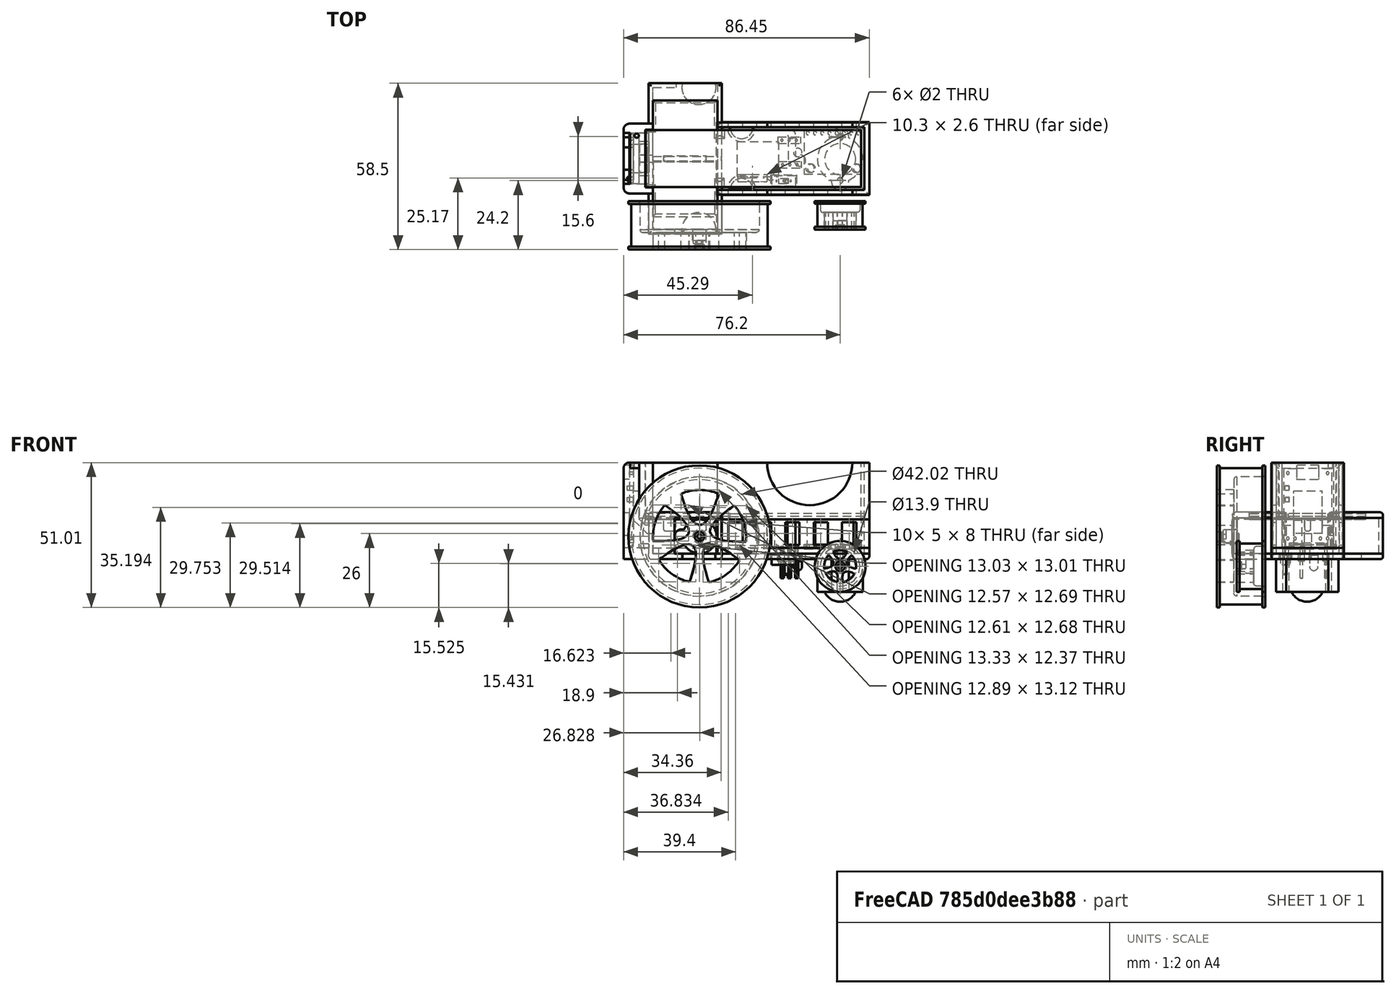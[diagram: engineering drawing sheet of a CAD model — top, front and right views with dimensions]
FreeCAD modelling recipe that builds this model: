
FCSTD DOCUMENT  (FreeCAD 0.18R16146 (Git))
Label: 01_Minibot
License: All rights reserved
LicenseURL: http://en.wikipedia.org/wiki/All_rights_reserved
objects: Part::Box×28, Part::Cylinder×24, Sketcher::SketchObject×20, Part::MultiFuse×20, PartDesign::Body×18, PartDesign::Pad×16, Part::Cut×8, Part::Fillet×7, Part::Chamfer×5, Image::ImagePlane×3, PartDesign::Revolution×2, PartDesign::Pocket×2, PartDesign::PolarPattern×2, Part::Sphere×2, Part::Feature×2, Mesh::Feature×2, Part::Extrusion×1, Part::Part2DObjectPython×1, Part::FeaturePython×1, PartDesign::FeatureBase×1, +1 more types
note: 180 computed .brp shape members not serialized (recipe doc carries the construction recipe); baked Part::Feature solids carry a one-line shape summary decoded from their .brp

FEATURE [Sketcher::SketchObject] Sketch
  MapMode = 5
  Support = -> [XY_Plane]
  sketch-geometry (4):
    g0: LineSegment StartX=-11.1288 StartY=11.9 StartZ=0 EndX=11.1288 EndY=11.9 EndZ=0
    g1: LineSegment StartX=11.1288 StartY=-11.9 StartZ=0 EndX=-11.1288 EndY=-11.9 EndZ=0
    g2: LineSegment StartX=-11.1288 StartY=-11.9 StartZ=0 EndX=-11.1288 EndY=11.9 EndZ=0
    g3: LineSegment StartX=11.1288 StartY=-11.9 StartZ=0 EndX=11.1288 EndY=11.9 EndZ=0
  constraints (9):
    c: Coincident(g0,g2)
    c: Coincident(g3,g1)
    c: Coincident(g3,g0)
    c: Coincident(g1,g2)
    c: Symmetric(g0,g0,g-2)
    c: Symmetric(g1,g0,g-1)
    c: DistanceY(g3,g3) = 23.8
    c: Horizontal(g1)
    c: Vertical(g2)
FEATURE [PartDesign::Pad] Pad
  Length = 12
  Length2 = 100
  Midplane = true
  Profile = -> Sketch
  Type = 0
FEATURE [PartDesign::Body] Body
  Group = -> [Sketch,Pad]
  Origin = -> Origin
  Tip = -> Pad
FEATURE [Sketcher::SketchObject] Sketch003
  MapMode = 5
  Placement = pos=(0,0,0) rot=(1,0,0;1.5708rad)
  Support = -> [XZ_Plane001]
  sketch-geometry (5):
    g0: ArcOfCircle CenterX=-5 CenterY=0 CenterZ=0 NormalX=0 NormalY=0 NormalZ=1 AngleXU=0 Radius=6 StartAngle=0.429754 EndAngle=5.85353
    g1: ArcOfCircle CenterX=1.3 CenterY=0 CenterZ=0 NormalX=0 NormalY=0 NormalZ=1 AngleXU=0 Radius=2.5 StartAngle=4.68906 EndAngle=7.86361
    g2: LineSegment StartX=1.27592 StartY=2.49988 StartZ=0 EndX=0.454409 EndY=2.49988 EndZ=0
    g3: LineSegment StartX=1.24168 StartY=-2.49932 StartZ=0 EndX=0.454668 EndY=-2.49932 EndZ=0
    g4: Circle CenterX=-5 CenterY=0 CenterZ=0 NormalX=0 NormalY=0 NormalZ=1 AngleXU=0 Radius=2.3
  constraints (14):
    c: PointOnObject(g0,g-1)
    c: Radius(g0) = 6
    c: DistanceX(g0) = -5
    c: PointOnObject(g1,g-1)
    c: Radius(g1) = 2.5
    c: DistanceX(g1) = 1.3
    c: Horizontal(g2)
    c: Horizontal(g3)
    c: Coincident(g1,g3)
    c: Coincident(g0,g3)
    c: Coincident(g1,g2)
    c: Coincident(g2,g0)
    c: Coincident(g4,g0)
    c: Radius(g4) = 2.3
FEATURE [PartDesign::Pad] Pad003
  Length = 2.4
  Length2 = 100
  Placement = pos=(0,0,0) rot=(1,0,0;1.5708rad)
  Profile = -> Sketch003
  Type = 0
FEATURE [PartDesign::Body] Body001
  Group = -> [Sketch003,Pad003]
  Origin = -> Origin001
  Placement = pos=(-0.22,13.6,0) rot=(0,0,1;0rad)
  Tip = -> Pad003
FEATURE [Part::Cylinder] Cylinder
  Angle = 360
  AttacherType = Attacher::AttachEngine3D
  Height = 3.2
  Placement = pos=(-5.22,13.6,-3e-15) rot=(-1,0,0;1.5708rad)
  Radius = 2.3
FEATURE [Part::MultiFuse] Fusion  label="Servo9gLeft"
  Placement = pos=(0,13,0) rot=(0,1,0;3.14159rad)
  Shapes = -> [Body,Body001,Cylinder]
FEATURE [Part::Box] Box  label="BatterySlot"
  AttacherType = Attacher::AttachEngine3D
  Height = 20
  Length = 75.8
  Placement = pos=(-13.755,-10,6.01) rot=(0,0,1;0rad)
  Width = 20
FEATURE [Sketcher::SketchObject] Sketch006
  MapMode = 5
  Support = -> [XY_Plane004]
  sketch-geometry (26):
    g0: LineSegment StartX=-13 StartY=8.50414 StartZ=0 EndX=14.2821 EndY=8.50414 EndZ=0
    g1: LineSegment StartX=14.2821 StartY=8.50414 StartZ=0 EndX=14.2821 EndY=6.5 EndZ=0
    g2: LineSegment StartX=14.2821 StartY=-8.50414 StartZ=0 EndX=-13 EndY=-8.50414 EndZ=0
    g3: LineSegment StartX=-13 StartY=-8.50414 StartZ=0 EndX=-13 EndY=-3.9 EndZ=0
    g4: LineSegment StartX=-14.2509 StartY=3.9 StartZ=0 EndX=-13 EndY=3.9 EndZ=0
    g5: LineSegment StartX=-13 StartY=-3.9 StartZ=0 EndX=-14.2509 EndY=-3.9 EndZ=0
    g6: LineSegment StartX=-14.2509 StartY=-3.9 StartZ=0 EndX=-14.2509 EndY=3.9 EndZ=0
    g7: LineSegment StartX=-13 StartY=3.9 StartZ=0 EndX=-13 EndY=8.50414 EndZ=0
    g8: LineSegment StartX=14.2821 StartY=6.5 StartZ=0 EndX=13 EndY=6.5 EndZ=0
    g9: LineSegment StartX=13 StartY=6.5 StartZ=0 EndX=13 EndY=-6.5 EndZ=0
    g10: LineSegment StartX=13 StartY=-6.5 StartZ=0 EndX=14.2821 EndY=-6.5 EndZ=0
    g11: LineSegment StartX=14.2821 StartY=-6.5 StartZ=0 EndX=14.2821 EndY=-8.50414 EndZ=0
    g12: Circle CenterX=-11.5 CenterY=7.00414 CenterZ=0 NormalX=0 NormalY=0 NormalZ=1 AngleXU=0 Radius=0.5
    g13: Circle CenterX=-11.5 CenterY=-7.00414 CenterZ=0 NormalX=0 NormalY=0 NormalZ=1 AngleXU=0 Radius=0.5
    g14: Circle CenterX=11.5 CenterY=7.00414 CenterZ=0 NormalX=0 NormalY=0 NormalZ=1 AngleXU=0 Radius=0.5
    g15: Circle CenterX=11.5 CenterY=4.46414 CenterZ=0 NormalX=0 NormalY=0 NormalZ=1 AngleXU=0 Radius=0.5
    g16: Circle CenterX=11.5 CenterY=-7.00414 CenterZ=0 NormalX=0 NormalY=0 NormalZ=1 AngleXU=0 Radius=0.5
    g17: Circle CenterX=11.5 CenterY=-4.46414 CenterZ=0 NormalX=0 NormalY=0 NormalZ=1 AngleXU=0 Radius=0.5
    g18: LineSegment StartX=-7 StartY=8.00414 StartZ=0 EndX=-5.5 EndY=8.00414 EndZ=0
    g19: LineSegment StartX=-5.5 StartY=8.00414 StartZ=0 EndX=-5.5 EndY=6.50414 EndZ=0
    g20: LineSegment StartX=-5.5 StartY=6.50414 StartZ=0 EndX=-7 EndY=6.50414 EndZ=0
    g21: LineSegment StartX=-7 StartY=6.50414 StartZ=0 EndX=-7 EndY=8.00414 EndZ=0
    g22: LineSegment StartX=-3 StartY=8 StartZ=0 EndX=-1.5 EndY=8 EndZ=0
    g23: LineSegment StartX=-1.5 StartY=8 StartZ=0 EndX=-1.5 EndY=6.5 EndZ=0
    g24: LineSegment StartX=-1.5 StartY=6.5 StartZ=0 EndX=-3 EndY=6.5 EndZ=0
    g25: LineSegment StartX=-3 StartY=6.5 StartZ=0 EndX=-3 EndY=8 EndZ=0
  constraints (68):
    c: Coincident(g0,g1)
    c: Coincident(g11,g2)
    c: Coincident(g2,g3)
    c: Coincident(g7,g0)
    c: Horizontal(g0)
    c: Horizontal(g2)
    c: Vertical(g1)
    c: Vertical(g3)
    c: Symmetric(g0,g11,g-1)
    c: Coincident(g5,g6)
    c: Coincident(g6,g4)
    c: Horizontal(g4)
    c: Horizontal(g5)
    c: Vertical(g6)
    c: Symmetric(g4,g5,g-1)
    c: DistanceX(g4) = -14.2509
    c: DistanceY(g4) = 3.9
    c: PointOnObject(g3,g5)
    c: PointOnObject(g7,g4)
    c: Tangent(g3,g7)
    c: Coincident(g8,g9)
    c: Coincident(g9,g10)
    c: Horizontal(g8)
    c: Horizontal(g10)
    c: Vertical(g9)
    c: Symmetric(g8,g9,g-1)
    c: Coincident(g1,g8)
    c: PointOnObject(g11,g10)
    c: Tangent(g1,g11)
    c: DistanceY(g12,g0) = 1.5
    c: Coincident(g4,g7)
    c: DistanceX(g4) = -13
    c: DistanceX(g0,g12) = 1.5
    c: Radius(g12) = 0.5
    c: Equal(g12,g13) = 0.5
    c: DistanceX(g2,g13) = 1.5
    c: Coincident(g3,g5)
    c: Equal(g2,g0)
    c: DistanceY(g2,g13) = 1.5
    c: Equal(g12,g14) = 0.5
    c: DistanceX(g13,g16) = 23
    c: Vertical(g16,g17)
    c: Vertical(g17,g15)
    c: Vertical(g15,g14)
    c: Horizontal(g12,g14)
    c: DistanceY(g14) = 7.00414
    c: DistanceY(g16,g17) = 2.54
    c: Horizontal(g13,g16)
    c: DistanceY(g15,g14) = 2.54
    c: Coincident(g18,g19)
    c: Coincident(g19,g20)
    c: Coincident(g20,g21)
    c: Coincident(g21,g18)
    c: Horizontal(g18)
    c: Horizontal(g20)
    c: Vertical(g19)
    c: Vertical(g21)
    c: Coincident(g22,g23)
    c: Coincident(g23,g24)
    c: Coincident(g24,g25)
    c: Coincident(g25,g22)
    c: Horizontal(g22)
    c: Horizontal(g24)
    c: Vertical(g23)
    c: Vertical(g25)
    c: DistanceX(g22,g22) = 1.5
    c: DistanceY(g23,g22) = 1.5
    c: Coincident(g10,g11)
FEATURE [Part::Box] Box001  label="Cube"
  AttacherType = Attacher::AttachEngine3D
  Height = 2.5
  Length = 5
  Placement = pos=(-14.25,-3.9,1) rot=(0,0,1;0rad)
  Width = 7.8
FEATURE [PartDesign::Pad] Pad006
  Length = 1.5
  Length2 = 100
  Profile = -> Sketch006
  Type = 0
FEATURE [PartDesign::Body] Body004
  Group = -> [Sketch006,Pad006]
  Origin = -> Origin004
  Tip = -> Pad006
FEATURE [Part::Box] Box002  label="Cube001"
  AttacherType = Attacher::AttachEngine3D
  Height = 1.5
  Length = 2.2
  Placement = pos=(-16.2,-8.005,17.3) rot=(0,0,1;0rad)
  Width = 1.5
FEATURE [Part::Box] Box003  label="Cube002"
  AttacherType = Attacher::AttachEngine3D
  Height = 1.5
  Length = 2.2
  Placement = pos=(-16.2,-8.005,13.3) rot=(0,0,1;0rad)
  Width = 1.5
FEATURE [Part::MultiFuse] Fusion002  label="Re"
  Placement = pos=(-14,-7e-15,11.8) rot=(0.707107,0,-0.707107;3.14159rad)
  Shapes = -> [Body004,Box001]
FEATURE [Part::MultiFuse] Fusion003  label="Recharger"
  Placement = pos=(-4,0,-1) rot=(0,0,1;0rad)
  Shapes = -> [Box002,Box003,Fusion002]
FEATURE [Image::ImagePlane] ImagePlane001
  Placement = pos=(24.2,0,0) rot=(0,0,1;4.71239rad)
  XSize = 80.52
  YSize = 85
FEATURE [Sketcher::SketchObject] Sketch009
  MapMode = 5
  Placement = pos=(0,0,0) rot=(0.57735,0.57735,0.57735;2.0944rad)
  Support = -> [YZ_Plane007]
  sketch-geometry (18):
    g0: LineSegment StartX=-32 StartY=25 StartZ=0 EndX=-31.0063 EndY=25 EndZ=0
    g1: LineSegment StartX=-15.9986 StartY=21.0096 StartZ=0 EndX=-25.0038 EndY=21.0096 EndZ=0
    g2: GeomPoint [constr] X=-32 Y=2 Z=0
    g3: GeomPoint [constr] X=-32 Y=21.9953 Z=0
    g4: LineSegment StartX=-15.9848 StartY=25 StartZ=0 EndX=-15.9848 EndY=24 EndZ=0
    g5: LineSegment StartX=-31.0063 StartY=24 StartZ=0 EndX=-31.0063 EndY=25 EndZ=0
    g6: LineSegment StartX=-15.9848 StartY=25 StartZ=0 EndX=-14.9848 EndY=25 EndZ=0
    g7: LineSegment StartX=-32 StartY=25 StartZ=0 EndX=-32 EndY=1.7 EndZ=0
    g8: LineSegment StartX=-30.3779 StartY=0.8 StartZ=0 EndX=-28.7779 EndY=0.8 EndZ=0
    g9: LineSegment StartX=-28.7779 StartY=0.8 StartZ=0 EndX=-28.7779 EndY=2.4 EndZ=0
    g10: LineSegment StartX=-28.7779 StartY=2.4 StartZ=0 EndX=-25.9779 EndY=2.4 EndZ=0
    g11: LineSegment StartX=-25.9779 StartY=2.4 StartZ=0 EndX=-25.9779 EndY=20.0103 EndZ=0
    g12: ArcOfCircle CenterX=-24.9498 CenterY=19.9825 CenterZ=0 NormalX=0 NormalY=0 NormalZ=1 AngleXU=0 Radius=1.02846 StartAngle=1.62331 EndAngle=3.11452
    g13: ArcOfCircle CenterX=-15.9716 CenterY=21.996 CenterZ=0 NormalX=0 NormalY=0 NormalZ=1 AngleXU=0 Radius=0.986789 StartAngle=4.68499 EndAngle=6.28489
    g14: LineSegment StartX=-14.9848 StartY=25 StartZ=0 EndX=-14.9848 EndY=21.9977 EndZ=0
    g15: LineSegment StartX=-32 StartY=1.7 StartZ=0 EndX=-30.3779 EndY=1.7 EndZ=0
    g16: LineSegment StartX=-30.3779 StartY=1.7 StartZ=0 EndX=-30.3779 EndY=0.8 EndZ=0
    g17: LineSegment StartX=-15.9848 StartY=24 StartZ=0 EndX=-31.0063 EndY=24 EndZ=0
  constraints (39):
    c: Horizontal(g0)
    c: Horizontal(g1)
    c: Coincident(g17,g5)
    c: Vertical(g4)
    c: Vertical(g5)
    c: Coincident(g0,g5)
    c: Vertical(g7)
    c: Horizontal(g8)
    c: Vertical(g9)
    c: Coincident(g10,g9)
    c: Horizontal(g10)
    c: Coincident(g10,g11)
    c: Coincident(g11,g12)
    c: Coincident(g1,g12)
    c: Coincident(g14,g6)
    c: Coincident(g14,g13)
    c: Vertical(g14)
    c: DistanceX(g0) = -32
    c: DistanceY(g0) = 25
    c: DistanceX(g4,g6) = 1
    c: DistanceY(g4,g4) = 1
    c: Coincident(g1,g13)
    c: Vertical(g11)
    c: Coincident(g4,g6)
    c: Horizontal(g6)
    c: DistanceY(g5,g5) = 1
    c: Coincident(g8,g9)
    c: DistanceY(g8) = 0.8
    c: Coincident(g15,g16)
    c: Horizontal(g15)
    c: Vertical(g16)
    c: Coincident(g16,g8)
    c: DistanceX(g8,g8) = 1.6
    c: DistanceY(g16,g16) = 0.9
    c: Coincident(g7,g15)
    c: DistanceX(g10,g10) = 2.8
    c: DistanceY(g10) = 2.4
    c: Coincident(g7,g0)
    c: Coincident(g17,g4)
FEATURE [PartDesign::Revolution] Revolution
  Angle = 360
  Axis = (1.129e-13,1,-1.129e-13)
  Base = (0,0,0)
  Placement = pos=(0,0,0) rot=(0.57735,0.57735,0.57735;2.0944rad)
  Profile = -> Sketch009
  ReferenceAxis = -> Sketch009 [H_Axis]
FEATURE [Sketcher::SketchObject] Sketch010
  Placement = pos=(-5.2,0,0) rot=(1,0,0;1.5708rad)
  sketch-geometry (4):
    g0: ArcOfParabola CenterX=5.21191 CenterY=4.0067 CenterZ=0 NormalX=0 NormalY=0 NormalZ=1 Focal=1.01065 AngleXU=1.56188 StartAngle=-6.6848 EndAngle=6.64864
    g1: GeomPoint X=5.22093 Y=5.0173 Z=0
    g2: LineSegment [constr] StartX=5.21191 StartY=4.0067 StartZ=0 EndX=5.22093 EndY=5.0173 EndZ=0
    g3: ArcOfCircle CenterX=5.32845 CenterY=-0.410138 CenterZ=0 NormalX=0 NormalY=0 NormalZ=1 AngleXU=0 Radius=16.7909 StartAngle=1.16251 EndAngle=1.97913
  constraints (6):
    c: InternalAlignment(g1,g0)
    c: Coincident(g1,g2)
    c: Coincident(g0,g2)
    c: PointOnObject(g3,g0)
    c: Coincident(g0,g3)
    c: Coincident(g3,g0)
FEATURE [PartDesign::Pocket] Pocket
  BaseFeature = -> Revolution
  Length = 5
  Length2 = 100
  Midplane = true
  Placement = pos=(0,0,0) rot=(0.57735,0.57735,0.57735;2.0944rad)
  Profile = -> Sketch010
  Type = 1
FEATURE [PartDesign::PolarPattern] PolarPattern
  Angle = 360
  Axis = -> Y_Axis007
  BaseFeature = -> Pocket
  Occurrences = 5
  Originals = -> [Pocket]
  Placement = pos=(0,0,0) rot=(0.57735,0.57735,0.57735;2.0944rad)
FEATURE [PartDesign::Body] Body007  label="02_Wheel"
  Group = -> [Sketch009,Revolution,Sketch010,Pocket,PolarPattern]
  Origin = -> Origin007
  Placement = pos=(5.2,0,0) rot=(0,0,1;0rad)
  Tip = -> PolarPattern
FEATURE [Sketcher::SketchObject] Sketch012
  MapMode = 5
  Support = -> [XY_Plane010]
  sketch-geometry (8):
    g0: LineSegment StartX=-11.1434 StartY=25 StartZ=0 EndX=-3.10416 EndY=25 EndZ=0
    g1: LineSegment StartX=-3.5631 StartY=-25 StartZ=0 EndX=-11.1434 EndY=-25 EndZ=0
    g2: LineSegment StartX=-11.1434 StartY=-25 StartZ=0 EndX=-11.1434 EndY=25 EndZ=0
    g3: LineSegment StartX=-12.6434 StartY=26.5 StartZ=0 EndX=-3.10416 EndY=26.5 EndZ=0
    g4: LineSegment StartX=-3.5631 StartY=-26.5 StartZ=0 EndX=-12.6434 EndY=-26.5 EndZ=0
    g5: LineSegment StartX=-12.6434 StartY=-26.5 StartZ=0 EndX=-12.6434 EndY=26.5 EndZ=0
    g6: LineSegment StartX=-3.5631 StartY=-25 StartZ=0 EndX=-3.5631 EndY=-26.5 EndZ=0
    g7: LineSegment StartX=-3.10416 StartY=26.5 StartZ=0 EndX=-3.10416 EndY=25 EndZ=0
  constraints (19):
    c: Coincident(g1,g2)
    c: Coincident(g2,g0)
    c: Horizontal(g0)
    c: Horizontal(g1)
    c: Vertical(g2)
    c: Coincident(g4,g5)
    c: Coincident(g5,g3)
    c: Horizontal(g3)
    c: Horizontal(g4)
    c: DistanceX(g3,g0) = 1.5
    c: DistanceY(g0,g3) = 1.5
    c: Vertical(g6)
    c: Coincident(g1,g6)
    c: Coincident(g4,g6)
    c: Vertical(g7)
    c: Coincident(g3,g7)
    c: Coincident(g0,g7)
    c: DistanceY(g4,g1) = 1.5
    c: Symmetric(g4,g3,g-1)
FEATURE [Sketcher::SketchObject] Sketch013
  MapMode = 5
  Support = -> [XY_Plane009]
  sketch-geometry (4):
    g0: LineSegment StartX=11.48 StartY=26.471 StartZ=0 EndX=11.48 EndY=8 EndZ=0
    g1: LineSegment StartX=12.98 StartY=26.471 StartZ=0 EndX=12.98 EndY=8 EndZ=0
    g2: LineSegment StartX=12.98 StartY=26.471 StartZ=0 EndX=11.48 EndY=26.471 EndZ=0
    g3: LineSegment StartX=11.48 StartY=8 StartZ=0 EndX=12.98 EndY=8 EndZ=0
  constraints (11):
    c: Vertical(g0)
    c: Vertical(g1)
    c: Coincident(g2,g1)
    c: Horizontal(g2)
    c: Coincident(g2,g0)
    c: Horizontal(g3)
    c: Coincident(g0,g3)
    c: Coincident(g1,g3)
    c: DistanceX(g0) = 11.48
    c: DistanceY(g0) = 8
    c: DistanceX(g2,g2) = 1.5
FEATURE [PartDesign::Pad] Pad010
  Length = 12.5
  Length2 = 100
  Profile = -> Sketch013
  Type = 0
FEATURE [PartDesign::Body] Body009
  Group = -> [Sketch013,Pad010]
  Origin = -> Origin009
  Tip = -> Pad010
FEATURE [PartDesign::Pad] Pad011
  Length = 12.5
  Length2 = 100
  Profile = -> Sketch012
  Type = 0
FEATURE [PartDesign::Body] Body010
  Group = -> [Sketch012,Pad011]
  Origin = -> Origin010
  Tip = -> Pad011
FEATURE [Part::Box] Box005  label="Cube003"
  AttacherType = Attacher::AttachEngine3D
  Height = 2
  Length = 25.7
  Placement = pos=(-12.5,-26.5,-8) rot=(0,0,1;0rad)
  Width = 53
FEATURE [Sketcher::SketchObject] Sketch016
  MapMode = 5
  Support = -> [XY_Plane013]
  sketch-geometry (10):
    g0: ArcOfCircle CenterX=56.3362 CenterY=0 CenterZ=0 NormalX=0 NormalY=0 NormalZ=1 AngleXU=0 Radius=8 StartAngle=3.52599 EndAngle=5.89879
    g1: ArcOfCircle CenterX=48.3362 CenterY=0 CenterZ=0 NormalX=0 NormalY=0 NormalZ=1 AngleXU=0 Radius=3 StartAngle=1.5708 EndAngle=4.71239
    g2: ArcOfCircle CenterX=64.3402 CenterY=0 CenterZ=0 NormalX=0 NormalY=0 NormalZ=1 AngleXU=0 Radius=3 StartAngle=4.71239 EndAngle=7.85532
    g3: LineSegment StartX=48.3362 StartY=-3 StartZ=0 EndX=48.92 EndY=-3 EndZ=0
    g4: LineSegment StartX=48.3362 StartY=3 StartZ=0 EndX=48.92 EndY=3 EndZ=0
    g5: ArcOfCircle CenterX=56.3362 CenterY=0 CenterZ=0 NormalX=0 NormalY=0 NormalZ=1 AngleXU=0 Radius=8 StartAngle=0.384396 EndAngle=2.7572
    g6: LineSegment StartX=63.7524 StartY=3 StartZ=0 EndX=64.3362 EndY=3 EndZ=0
    g7: LineSegment StartX=63.7524 StartY=-3 StartZ=0 EndX=64.3402 EndY=-3 EndZ=0
    g8: Circle CenterX=48.8362 CenterY=0 CenterZ=0 NormalX=0 NormalY=0 NormalZ=1 AngleXU=0 Radius=1
    g9: Circle CenterX=63.8362 CenterY=0 CenterZ=0 NormalX=0 NormalY=0 NormalZ=1 AngleXU=0 Radius=1
  constraints (26):
    c: PointOnObject(g0,g-1)
    c: Radius(g0) = 8
    c: Tangent(g1,g4) = 1.5708
    c: Tangent(g1,g3) = -1.5708
    c: Coincident(g7,g2) = -1.5708
    c: Coincident(g6,g2) = 1.5708
    c: Horizontal(g3)
    c: Equal(g1,g2)
    c: PointOnObject(g1,g-1)
    c: DistanceX(g0,g2) = 8
    c: DistanceY(g1,g1) = 6
    c: DistanceX(g1,g0) = 8
    c: Equal(g0,g5)
    c: Coincident(g0,g5)
    c: Coincident(g4,g5)
    c: Coincident(g6,g5)
    c: Tangent(g4,g6)
    c: Coincident(g3,g0)
    c: Coincident(g7,g0)
    c: Tangent(g3,g7)
    c: PointOnObject(g8,g-1)
    c: PointOnObject(g9,g-1)
    c: DistanceX(g8,g9) = 15
    c: Distance(g0,g9) = 7.5
    c: Radius(g8) = 1
    c: Radius(g9) = 1
FEATURE [PartDesign::Pad] Pad014
  Length = 11.5
  Length2 = 100
  Profile = -> Sketch016
  Reversed = true
  Type = 0
FEATURE [PartDesign::Body] Body013
  Group = -> [Sketch016,Pad014]
  Origin = -> Origin013
  Tip = -> Pad014
FEATURE [Part::Sphere] Sphere
  Angle1 = -90
  Angle2 = 90
  Angle3 = 360
  AttacherType = Attacher::AttachEngine3D
  Placement = pos=(56.3,0,-9) rot=(0,0,1;0rad)
  Radius = 6
FEATURE [Part::MultiFuse] Fusion006  label="CasterWheel"
  Placement = pos=(54.7,-56.5,-8) rot=(0,0,1;1.5708rad)
  Shapes = -> [Body013,Sphere]
FEATURE [Image::ImagePlane] ImagePlane  label="Recharger_IMG"
  Placement = pos=(-17.5,0,12) rot=(-0.707107,0,0.707107;3.14159rad)
  XSize = 28.5
  YSize = 17
FEATURE [Sketcher::SketchObject] Sketch017
  MapMode = 5
  Support = -> [XY_Plane014]
  sketch-geometry (14):
    g0: LineSegment StartX=21.0792 StartY=7.8 StartZ=0 EndX=41.2792 EndY=7.8 EndZ=0
    g1: LineSegment StartX=41.2792 StartY=7.8 StartZ=0 EndX=41.2792 EndY=-7.8 EndZ=0
    g2: LineSegment StartX=41.2792 StartY=-7.8 StartZ=0 EndX=21.0792 EndY=-7.8 EndZ=0
    g3: LineSegment StartX=21.0792 StartY=-7.8 StartZ=0 EndX=21.0792 EndY=7.8 EndZ=0
    g4: Circle CenterX=23.0792 CenterY=5.78 CenterZ=0 NormalX=0 NormalY=0 NormalZ=1 AngleXU=0 Radius=1.5
    g5: Circle CenterX=39.2792 CenterY=5.78 CenterZ=0 NormalX=0 NormalY=0 NormalZ=1 AngleXU=0 Radius=1.5
    g6: Circle CenterX=40.1024 CenterY=-6.5659 CenterZ=0 NormalX=0 NormalY=0 NormalZ=1 AngleXU=0 Radius=0.6
    g7: Circle CenterX=37.5624 CenterY=-6.5659 CenterZ=0 NormalX=0 NormalY=0 NormalZ=1 AngleXU=0 Radius=0.6
    g8: Circle CenterX=35.0224 CenterY=-6.5659 CenterZ=0 NormalX=0 NormalY=0 NormalZ=1 AngleXU=0 Radius=0.6
    g9: Circle CenterX=32.4824 CenterY=-6.5659 CenterZ=0 NormalX=0 NormalY=0 NormalZ=1 AngleXU=0 Radius=0.6
    g10: Circle CenterX=29.9424 CenterY=-6.5659 CenterZ=0 NormalX=0 NormalY=0 NormalZ=1 AngleXU=0 Radius=0.6
    g11: Circle CenterX=27.4024 CenterY=-6.5659 CenterZ=0 NormalX=0 NormalY=0 NormalZ=1 AngleXU=0 Radius=0.6
    g12: Circle CenterX=24.8624 CenterY=-6.5659 CenterZ=0 NormalX=0 NormalY=0 NormalZ=1 AngleXU=0 Radius=0.6
    g13: Circle CenterX=22.3224 CenterY=-6.5659 CenterZ=0 NormalX=0 NormalY=0 NormalZ=1 AngleXU=0 Radius=0.6
  constraints (39):
    c: Coincident(g0,g1)
    c: Coincident(g1,g2)
    c: Coincident(g2,g3)
    c: Coincident(g3,g0)
    c: Horizontal(g0)
    c: Horizontal(g2)
    c: Vertical(g1)
    c: Vertical(g3)
    c: Symmetric(g0,g2,g-1)
    c: DistanceY(g0) = 7.8
    c: DistanceX(g0,g0) = 20.2
    c: Radius(g4) = 1.5
    c: Equal(g4,g5) = 1.5
    c: Distance(g4,g3) = 2
    c: Distance(g5,g1) = 2
    c: Distance(g4,g0) = 2.02
    c: Distance(g5,g0) = 2.02
    c: Radius(g6) = 0.6
    c: Radius(g7) = 0.6
    c: DistanceX(g7,g6) = 2.54
    c: DistanceY(g6,g7) = 0
    c: Equal(g6,g8) = 0.5
    c: Equal(g7,g9) = 0.5
    c: DistanceX(g9,g8) = 2.54
    c: DistanceY(g8,g9) = 0
    c: DistanceX(g8,g7) = 2.54
    c: Equal(g6,g10) = 0.5
    c: Equal(g7,g11) = 0.5
    c: DistanceX(g11,g10) = 2.54
    c: DistanceY(g10,g11) = 0
    c: Equal(g10,g12) = 0.5
    c: Equal(g11,g13) = 0.5
    c: DistanceX(g13,g12) = 2.54
    c: DistanceY(g12,g13) = 0
    c: DistanceX(g12,g11) = 2.54
    c: DistanceX(g10,g9) = 2.54
    c: DistanceY(g7,g8) = 0
    c: DistanceY(g9,g10) = 0
    c: DistanceY(g12,g11) = 0
FEATURE [PartDesign::Pad] Pad015
  Length = 1.5
  Length2 = 100
  Profile = -> Sketch017
  Reversed = true
  Type = 0
FEATURE [PartDesign::Body] Body014  label="MPU6050"
  Group = -> [Sketch017,Pad015]
  Origin = -> Origin014
  Placement = pos=(21,2.4,-4.4) rot=(1,0,0;3.14159rad)
  Tip = -> Pad015
FEATURE [Image::ImagePlane] ImagePlane002  label="MPU6050_IMG"
  Placement = pos=(31.2,0,-1.6) rot=(0.707107,0.707107,0;3.14159rad)
  XSize = 15.5
  YSize = 20.2
FEATURE [Part::Box] Box007  label="ESP8266-07"
  AttacherType = Attacher::AttachEngine3D
  Height = 1
  Length = 14.7
  Placement = pos=(18.3447,6,-3.08993) rot=(1,0,0;3.14159rad)
  Width = 12.4
FEATURE [Sketcher::SketchObject] Sketch018
  MapMode = 5
  Support = -> [XY_Plane015]
  sketch-geometry (4):
    g0: LineSegment StartX=12.98 StartY=-8 StartZ=0 EndX=11.48 EndY=-8 EndZ=0
    g1: LineSegment StartX=11.48 StartY=-8 StartZ=0 EndX=11.48 EndY=-26.506 EndZ=0
    g2: LineSegment StartX=12.98 StartY=-8 StartZ=0 EndX=12.98 EndY=-26.506 EndZ=0
    g3: LineSegment StartX=11.48 StartY=-26.506 StartZ=0 EndX=12.98 EndY=-26.506 EndZ=0
  constraints (11):
    c: Horizontal(g0)
    c: Coincident(g0,g1)
    c: Coincident(g3,g1)
    c: Coincident(g3,g2)
    c: Horizontal(g3)
    c: Coincident(g0,g2)
    c: DistanceX(g0) = 11.48
    c: DistanceY(g0) = -8
    c: Vertical(g1)
    c: DistanceX(g0,g0) = 1.5
    c: Vertical(g2)
FEATURE [PartDesign::Pad] Pad016
  Length = 12.5
  Length2 = 100
  Profile = -> Sketch018
  Type = 0
FEATURE [PartDesign::Body] Body015
  Group = -> [Sketch018,Pad016]
  Origin = -> Origin015
  Tip = -> Pad016
FEATURE [Part::MultiFuse] Fusion007
  Placement = pos=(0,0,-6) rot=(0,0,1;0rad)
  Shapes = -> [Body015,Body009,Body010]
FEATURE [Part::Box] Box014  label="Cube011"
  AttacherType = Attacher::AttachEngine3D
  Height = 2
  Length = 24.23
  Placement = pos=(-11.25,-0.8,-6) rot=(0,0,1;0rad)
  Width = 1.6
FEATURE [Part::Box] Box015  label="Cube012"
  AttacherType = Attacher::AttachEngine3D
  Height = 5
  Length = 24.23
  Placement = pos=(-16,-1.25,-4) rot=(0,0,1;0rad)
  Width = 2.5
FEATURE [Part::Fillet] Fillet
  Base = -> Box005
  Edges = 4 edges r=1: [Edge4,Edge8,Edge9,Edge11]
  Placement = pos=(-0.2,0,0) rot=(0,0,1;0rad)
FEATURE [Part::Box] Box016  label="Cube013"
  AttacherType = Attacher::AttachEngine3D
  Height = 10
  Length = 2
  Placement = pos=(-18,-4.99,6) rot=(0,0,1;0rad)
  Width = 10
FEATURE [Part::Box] Box017  label="Cube014"
  AttacherType = Attacher::AttachEngine3D
  Height = 1.95
  Length = 3.2
  Placement = pos=(-19.2,-12.33,24.05) rot=(0,0,1;0rad)
  Width = 24.54
FEATURE [Sketcher::SketchObject] Sketch019
  MapMode = 5
  Placement = pos=(0,0,0) rot=(0.57735,0.57735,0.57735;2.0944rad)
  Support = -> [YZ_Plane016]
  sketch-geometry (9):
    g0: LineSegment StartX=9 StartY=26 StartZ=0 EndX=9 EndY=-3.93885 EndZ=0
    g1: LineSegment StartX=9 StartY=-3.93885 StartZ=0 EndX=-9 EndY=-3.93885 EndZ=0
    g2: LineSegment StartX=-9 StartY=-3.93885 StartZ=0 EndX=-9 EndY=26 EndZ=0
    g3: LineSegment StartX=-12.3284 StartY=26 StartZ=0 EndX=-9 EndY=26 EndZ=0
    g4: LineSegment StartX=12.2099 StartY=26 StartZ=0 EndX=12.2099 EndY=-8 EndZ=0
    g5: LineSegment StartX=12.2099 StartY=-8 StartZ=0 EndX=-12.3284 EndY=-8 EndZ=0
    g6: LineSegment StartX=-12.3284 StartY=-8 StartZ=0 EndX=-12.3284 EndY=26 EndZ=0
    g7: LineSegment StartX=9 StartY=26 StartZ=0 EndX=12.2099 EndY=26 EndZ=0
    g8: LineSegment StartX=-9 StartY=0 StartZ=0 EndX=-8.49201 EndY=0 EndZ=0
  constraints (20):
    c: Coincident(g0,g1)
    c: Horizontal(g1)
    c: Vertical(g0)
    c: Vertical(g2)
    c: Symmetric(g2,g0,g-2)
    c: DistanceY(g2) = 26
    c: Coincident(g7,g4)
    c: Coincident(g4,g5)
    c: Coincident(g5,g6)
    c: Coincident(g6,g3)
    c: Horizontal(g3)
    c: Horizontal(g5)
    c: Vertical(g4)
    c: Vertical(g6)
    c: PointOnObject(g3,g2)
    c: PointOnObject(g7,g0)
    c: Tangent(g3,g7)
    c: Coincident(g0,g7)
    c: PointOnObject(g8,g2)
    c: Coincident(g1,g2)
FEATURE [PartDesign::Pad] Pad017
  Length = 5.5
  Length2 = 100
  Placement = pos=(0,0,0) rot=(0.57735,0.57735,0.57735;2.0944rad)
  Profile = -> Sketch019
  Type = 0
FEATURE [PartDesign::Body] Body016
  Group = -> [Sketch019,Pad017]
  Origin = -> Origin016
  Placement = pos=(-21.5,0,0) rot=(0,0,1;0rad)
  Tip = -> Pad017
FEATURE [Part::Box] Box019  label="Cube016"
  AttacherType = Attacher::AttachEngine3D
  Height = 8
  Length = 2
  Placement = pos=(-21.5,-9,0.45) rot=(0,0,1;0rad)
  Width = 1.5
FEATURE [Part::Box] Box020  label="Cube017"
  AttacherType = Attacher::AttachEngine3D
  Height = 8
  Length = 2
  Placement = pos=(-21.5,7.5,0.45) rot=(0,0,1;0rad)
  Width = 1.5
FEATURE [Part::MultiFuse] Fusion008  label="RechargerSupport"
  Shapes = -> [Box020,Box019,Body016,Box017,Box016]
FEATURE [Part::Feature] Face
  shape: bbox 2e-07 x 24.54 x 31.8 mm, 1 faces, 0 solids (baked)
FEATURE [Part::Extrusion] Extrusion
  Base = -> Face
  Dir = (4.5,0,0)
  DirMode = 0
  FaceMakerClass = Part::FaceMakerBullseye
  LengthFwd = 0
  LengthRev = 0
  Solid = true
  Symmetric = false
FEATURE [Part::Part2DObjectPython] Rectangle  # Draft 2D object (typed FeaturePython)
  ChamferSize = 0
  Columns = 1
  FilletRadius = 0
  Height = 26.8106
  Length = 16.3775
  MakeFace = true
  Placement = pos=(-23.2993,-13.6958,6.5) rot=(0,0,1;0rad)
  Rows = 1
FEATURE [Part::Box] Box021  label="Cube018"
  AttacherType = Attacher::AttachEngine3D
  Height = 5
  Length = 5.5
  Placement = pos=(-18,-8.99,1) rot=(0,0,1;0rad)
  Width = 10
FEATURE [Part::Chamfer] Chamfer
  Base = -> Box021
  Edges = 1 edges r=4.8: [Edge4]
  Placement = pos=(0,4,0) rot=(0,0,1;0rad)
FEATURE [Part::Box] Box022  label="Cube019"
  AttacherType = Attacher::AttachEngine3D
  Height = 29
  Length = 22.74
  Placement = pos=(-11.26,-20.5,0) rot=(0,0,1;0rad)
  Width = 41
FEATURE [Part::Box] Box024  label="Cube021"
  AttacherType = Attacher::AttachEngine3D
  Height = 2
  Length = 25.7
  Placement = pos=(-12.5,-26.5,-8) rot=(0,0,1;0rad)
  Width = 53
FEATURE [Part::Fillet] Fillet003
  Base = -> Box024
  Edges = 4 edges r=1: [Edge4,Edge8,Edge9,Edge11]
  Placement = pos=(-0.2,0,0.5) rot=(1,0,0;3.14159rad)
FEATURE [Part::Cylinder] Cylinder009
  Angle = 360
  AttacherType = Attacher::AttachEngine3D
  Height = 25
  Placement = pos=(-16.9,8,3) rot=(0,0,1;0rad)
  Radius = 0.75
FEATURE [Part::Feature] CutVolume
  shape: bbox 9.221 x 27 x 18.3 mm, 6 faces (baked)
FEATURE [Part::Cut] CutPlane
  Base = -> Extrusion
  Tool = -> CutVolume
FEATURE [Part::MultiFuse] Fusion013
  Shapes = -> [Fusion008,Chamfer,CutPlane]
FEATURE [Part::Cut] Cut005
  Base = -> Fusion013
  Placement = pos=(0,0.06,0) rot=(0,0,1;0rad)
  Tool = -> Cylinder009
FEATURE [Sketcher::SketchObject] Sketch011
  MapMode = 5
  Support = -> [XY_Plane008]
  sketch-geometry (8):
    g0: LineSegment StartX=11.488 StartY=11 StartZ=0 EndX=63.2 EndY=11 EndZ=0
    g1: LineSegment StartX=63.2 StartY=11 StartZ=0 EndX=63.2 EndY=-11 EndZ=0
    g2: LineSegment StartX=63.2 StartY=-11 StartZ=0 EndX=11.488 EndY=-11 EndZ=0
    g3: LineSegment StartX=11.488 StartY=12.75 StartZ=0 EndX=64.95 EndY=12.75 EndZ=0
    g4: LineSegment StartX=64.95 StartY=12.75 StartZ=0 EndX=64.95 EndY=-12.75 EndZ=0
    g5: LineSegment StartX=64.95 StartY=-12.75 StartZ=0 EndX=11.488 EndY=-12.75 EndZ=0
    g6: LineSegment StartX=11.488 StartY=12.75 StartZ=0 EndX=11.488 EndY=11 EndZ=0
    g7: LineSegment StartX=11.488 StartY=-12.75 StartZ=0 EndX=11.488 EndY=-11 EndZ=0
  constraints (21):
    c: Coincident(g0,g1)
    c: Coincident(g1,g2)
    c: Horizontal(g0)
    c: Horizontal(g2)
    c: Vertical(g1)
    c: Coincident(g3,g4)
    c: Coincident(g4,g5)
    c: Horizontal(g3)
    c: Horizontal(g5)
    c: Vertical(g4)
    c: DistanceX(g1) = 63.2
    c: DistanceX(g1,g4) = 1.75
    c: DistanceY(g4,g1) = 1.75
    c: DistanceY(g0) = 11
    c: Symmetric(g0,g2,g-1)
    c: Symmetric(g3,g5,g-1)
    c: Coincident(g6,g3)
    c: Coincident(g6,g0)
    c: Vertical(g6)
    c: Coincident(g7,g5)
    c: Coincident(g7,g2)
FEATURE [PartDesign::Pad] Pad009
  Length = 20
  Length2 = 100
  Profile = -> Sketch011
  Type = 0
FEATURE [PartDesign::Body] Body008
  Group = -> [Sketch011,Pad009]
  Origin = -> Origin008
  Placement = pos=(0,0,6) rot=(0,0,1;0rad)
  Tip = -> Pad009
FEATURE [Part::MultiFuse] Fusion014
  Shapes = -> [Fillet003,Body008]
FEATURE [Part::Cylinder] Cylinder010
  Angle = 360
  AttacherType = Attacher::AttachEngine3D
  Height = 20
  Placement = pos=(5,-25,-11) rot=(0,0,1;0rad)
  Radius = 6
FEATURE [Part::Cylinder] Cylinder011
  Angle = 360
  AttacherType = Attacher::AttachEngine3D
  Height = 20
  Placement = pos=(5,25,-11) rot=(0,0,1;0rad)
  Radius = 6
FEATURE [Part::MultiFuse] Fusion015
  Shapes = -> [Cylinder010,Cylinder011]
FEATURE [Part::Cut] Cut007
  Base = -> Fillet
  Tool = -> Fusion015
FEATURE [Part::Box] Box026  label="Cube023"
  AttacherType = Attacher::AttachEngine3D
  Height = 2
  Length = 16
  Placement = pos=(11.48,8,-6) rot=(0,0,-1;1.5708rad)
  Width = 1.5
FEATURE [Part::Cylinder] Cylinder014
  Angle = 360
  AttacherType = Attacher::AttachEngine3D
  Height = 11.2
  Placement = pos=(-46,-6,1.1) rot=(-1,0,0;1.5708rad)
  Radius = 0.4
FEATURE [Part::Box] Box031  label="Cube027"
  AttacherType = Attacher::AttachEngine3D
  Height = 2.2
  Length = 8
  Placement = pos=(-52.54,0,0) rot=(0,0,1;0rad)
  Width = 2.4
FEATURE [Part::Cylinder] Cylinder015
  Angle = 360
  AttacherType = Attacher::AttachEngine3D
  Height = 11.2
  Placement = pos=(-48.54,-6,1.1) rot=(-1,0,0;1.5708rad)
  Radius = 0.4
FEATURE [Part::Fillet] Fillet005
  Base = -> Box014
  Edges = 2 edges r=0.5: [Edge10,Edge12]
FEATURE [Sketcher::SketchObject] Sketch022
  MapMode = 5
  Placement = pos=(0,0,0) rot=(1,0,0;1.5708rad)
  Support = -> [XZ_Plane019]
  sketch-geometry (8):
    g0: LineSegment StartX=-4.25 StartY=1.75 StartZ=0 EndX=4.25 EndY=1.75 EndZ=0
    g1: LineSegment StartX=4.25 StartY=1.75 StartZ=0 EndX=4.25 EndY=-1.75 EndZ=0
    g2: LineSegment StartX=4.25 StartY=-1.75 StartZ=0 EndX=-4.25 EndY=-1.75 EndZ=0
    g3: LineSegment StartX=-4.25 StartY=-1.75 StartZ=0 EndX=-4.25 EndY=1.75 EndZ=0
    g4: LineSegment StartX=-1.8 StartY=0.82 StartZ=0 EndX=1.8 EndY=0.82 EndZ=0
    g5: LineSegment StartX=1.8 StartY=0.82 StartZ=0 EndX=1.8 EndY=-0.82 EndZ=0
    g6: LineSegment StartX=1.8 StartY=-0.82 StartZ=0 EndX=-1.8 EndY=-0.82 EndZ=0
    g7: LineSegment StartX=-1.8 StartY=-0.82 StartZ=0 EndX=-1.8 EndY=0.82 EndZ=0
  constraints (24):
    c: Coincident(g0,g1)
    c: Coincident(g1,g2)
    c: Coincident(g2,g3)
    c: Coincident(g3,g0)
    c: Horizontal(g0)
    c: Horizontal(g2)
    c: Vertical(g1)
    c: Vertical(g3)
    c: Symmetric(g0,g2,g-1)
    c: Symmetric(g0,g0,g-2)
    c: DistanceY(g3,g3) = 3.5
    c: DistanceX(g2,g2) = 8.5
    c: Coincident(g4,g5)
    c: Coincident(g5,g6)
    c: Coincident(g6,g7)
    c: Coincident(g7,g4)
    c: Horizontal(g4)
    c: Horizontal(g6)
    c: Vertical(g5)
    c: Vertical(g7)
    c: Symmetric(g4,g4,g-2)
    c: Symmetric(g6,g4,g-1)
    c: DistanceX(g4,g4) = 3.6
    c: DistanceY(g5,g5) = 1.64
FEATURE [PartDesign::Pad] Pad020
  Length = 3.5
  Length2 = 100
  Placement = pos=(0,0,0) rot=(1,0,0;1.5708rad)
  Profile = -> Sketch022
  Type = 0
FEATURE [PartDesign::Body] Body019
  Group = -> [Sketch022,Pad020]
  Origin = -> Origin019
  Tip = -> Pad020
FEATURE [Part::Box] Box049  label="Cube045"
  AttacherType = Attacher::AttachEngine3D
  Height = 1.5
  Length = 1.5
  Placement = pos=(0.3,-7,-0.75) rot=(0,0,1;0rad)
  Width = 7
FEATURE [Part::Chamfer] Chamfer004
  Base = -> Box049
  Edges = 4 edges r=0.3: [Edge1,Edge5,Edge9,Edge10]
FEATURE [Part::Cylinder] Cylinder030
  Angle = 360
  AttacherType = Attacher::AttachEngine3D
  Height = 3.7
  Placement = pos=(0,-0.05,0) rot=(-1,0,0;1.5708rad)
  Radius = 0.25
FEATURE [Part::Cylinder] Cylinder031
  Angle = 360
  AttacherType = Attacher::AttachEngine3D
  Height = 3.7
  Placement = pos=(2.5,-0.05,0) rot=(-1,0,0;1.5708rad)
  Radius = 0.25
FEATURE [Part::Cylinder] Cylinder032
  Angle = 360
  AttacherType = Attacher::AttachEngine3D
  Height = 3.7
  Placement = pos=(-2.5,-0.05,0) rot=(-1,0,0;1.5708rad)
  Radius = 0.25
FEATURE [Part::MultiFuse] Fusion033  label="SlideSwitch"
  Placement = pos=(34.8,-7.9,-0.8) rot=(1,0,0;1.5708rad)
  Shapes = -> [Body019,Cylinder030,Chamfer004,Cylinder032,Cylinder031]
FEATURE [Mesh::Feature] SmartCars  label="SmartCars_V01"
  Placement = pos=(132.5,151,-1.7) rot=(0,0,1;4.71239rad)
FEATURE [Part::Cylinder] Cylinder033
  Angle = 360
  AttacherType = Attacher::AttachEngine3D
  Height = 11.2
  Placement = pos=(-51.08,-6,1.1) rot=(-1,0,0;1.5708rad)
  Radius = 0.4
FEATURE [Part::MultiFuse] Fusion034  label="PinsBarA"
  Placement = pos=(85.28,7.57,-3) rot=(1,0,0;1.5708rad)
  Shapes = -> [Box031,Cylinder033,Cylinder014,Cylinder015]
FEATURE [Part::Cylinder] Cylinder034
  Angle = 360
  AttacherType = Attacher::AttachEngine3D
  Height = 11.2
  Placement = pos=(-51.08,-6,1.1) rot=(-1,0,0;1.5708rad)
  Radius = 0.4
FEATURE [Part::Cylinder] Cylinder035
  Angle = 360
  AttacherType = Attacher::AttachEngine3D
  Height = 11.2
  Placement = pos=(-46,-6,1.1) rot=(-1,0,0;1.5708rad)
  Radius = 0.4
FEATURE [Part::Box] Box050  label="Cube046"
  AttacherType = Attacher::AttachEngine3D
  Height = 2.2
  Length = 8
  Placement = pos=(-52.54,0,0) rot=(0,0,1;0rad)
  Width = 2.4
FEATURE [Part::Cylinder] Cylinder036
  Angle = 360
  AttacherType = Attacher::AttachEngine3D
  Height = 11.2
  Placement = pos=(-48.54,-6,1.1) rot=(-1,0,0;1.5708rad)
  Radius = 0.4
FEATURE [Part::MultiFuse] Fusion035  label="PinsBarB"
  Placement = pos=(85.54,-1.07,-3) rot=(1,0,0;1.5708rad)
  Shapes = -> [Box050,Cylinder034,Cylinder035,Cylinder036]
FEATURE [Part::Cylinder] Cylinder037
  Angle = 360
  AttacherType = Attacher::AttachEngine3D
  Height = 4
  Placement = pos=(39.8,2.1,2.8) rot=(0,0,1;0rad)
  Radius = 1.5
FEATURE [Part::Sphere] Sphere001
  Angle1 = -90
  Angle2 = 90
  Angle3 = 360
  AttacherType = Attacher::AttachEngine3D
  Placement = pos=(39.8,2.1,6.8) rot=(0,0,1;0rad)
  Radius = 1.5
FEATURE [Part::MultiFuse] Fusion036  label="LED"
  Placement = pos=(0,4.25,2) rot=(1,0,0;3.14159rad)
  Shapes = -> [Cylinder037,Sphere001]
FEATURE [Part::MultiFuse] Fusion037
  Placement = pos=(0,0,-5.7) rot=(0,0,1;0rad)
  Shapes = -> [Fusion033,Fusion034,Fusion035,Fusion036]
FEATURE [Part::Box] Box051  label="Cube047"
  AttacherType = Attacher::AttachEngine3D
  Height = 10
  Length = 10.3
  Placement = pos=(18.64,-8.13,-14) rot=(0,0,1;0rad)
  Width = 2.6
FEATURE [Part::Box] Box052  label="Cube048"
  AttacherType = Attacher::AttachEngine3D
  Height = 10
  Length = 8.4
  Placement = pos=(36.4,7.23,-14) rot=(0,0,-1;1.5708rad)
  Width = 2.6
FEATURE [Part::Cylinder] Cylinder038
  Angle = 360
  AttacherType = Attacher::AttachEngine3D
  Height = 10
  Placement = pos=(40.55,-0.67,-14) rot=(0,0,1;0rad)
  Radius = 2
FEATURE [Part::Box] Box053  label="Cube049"
  AttacherType = Attacher::AttachEngine3D
  Height = 10
  Length = 9.2
  Placement = pos=(30.2,-9.97,-14) rot=(0,0,1;0rad)
  Width = 4.2
FEATURE [Sketcher::SketchObject] Sketch023
  MapMode = 5
  Support = -> [XY_Plane020]
  expr: Constraints[9] = Sketch011.Constraints[10]
  expr: Constraints[10] = Sketch011.Constraints[11]
  sketch-geometry (8):
    g0: LineSegment StartX=13 StartY=11.0423 StartZ=0 EndX=63.2 EndY=11.0423 EndZ=0
    g1: LineSegment StartX=63.2 StartY=11.0423 StartZ=0 EndX=63.2 EndY=-10.9577 EndZ=0
    g2: LineSegment StartX=63.2 StartY=-10.9577 StartZ=0 EndX=13.0435 EndY=-10.9577 EndZ=0
    g3: LineSegment StartX=13 StartY=12.7923 StartZ=0 EndX=64.95 EndY=12.7923 EndZ=0
    g4: LineSegment StartX=64.95 StartY=12.7923 StartZ=0 EndX=64.95 EndY=-12.7923 EndZ=0
    g5: LineSegment StartX=64.95 StartY=-12.7923 StartZ=0 EndX=13.0435 EndY=-12.7923 EndZ=0
    g6: LineSegment StartX=13 StartY=12.7923 StartZ=0 EndX=13 EndY=11.0423 EndZ=0
    g7: LineSegment StartX=13.0435 StartY=-12.7923 StartZ=0 EndX=13.0435 EndY=-10.9577 EndZ=0
  constraints (20):
    c: Coincident(g0,g1)
    c: Coincident(g1,g2)
    c: Horizontal(g0)
    c: Horizontal(g2)
    c: Vertical(g1)
    c: Coincident(g3,g4)
    c: Coincident(g4,g5)
    c: Horizontal(g3)
    c: Horizontal(g5)
    c: DistanceX(g1) = 63.2
    c: DistanceX(g1,g4) = 1.75
    c: Vertical(g6)
    c: Vertical(g7)
    c: Coincident(g2,g7)
    c: Coincident(g5,g7)
    c: Coincident(g0,g6)
    c: Coincident(g3,g6)
    c: DistanceY(g1,g1) = 22
    c: DistanceY(g6,g6) = 1.75
    c: Symmetric(g4,g3,g-1)
FEATURE [PartDesign::Pad] Pad021
  Length = 12
  Length2 = 100
  Profile = -> Sketch023
  Type = 0
FEATURE [PartDesign::Body] Body020
  Group = -> [Sketch023,Pad021]
  Origin = -> Origin020
  Placement = pos=(0,0,-6) rot=(0,0,1;0rad)
  Tip = -> Pad021
FEATURE [Part::Box] Box054  label="Cube050"
  AttacherType = Attacher::AttachEngine3D
  Height = 2.5
  Length = 3.25
  Placement = pos=(-16,-10.5,4) rot=(0,0,1;0rad)
  Width = 21
FEATURE [Part::Chamfer] Chamfer005
  Base = -> Box054
  Edges = 1 edges r=2.1: [Edge4]
FEATURE [Part::Fillet] Fillet006
  Base = -> Cut005
  Edges = 4 edges r=2: [Edge21,Edge22,Edge25,Edge27]
FEATURE [Part::MultiFuse] Fusion039
  Shapes = -> [Fillet006,Fusion007]
FEATURE [Part::Cut] Cut010
  Base = -> Fusion039
  Tool = -> Box015
FEATURE [Mesh::Feature] SmartCars001  label="SmartCars_v02"
  Placement = pos=(132.5,151,-5.2) rot=(0,0,1;4.71239rad)
FEATURE [Part::MultiFuse] Fusion040
  Shapes = -> [Box053,Box052,Cylinder038,Box051]
FEATURE [Part::Cylinder] Cylinder039
  Angle = 360
  AttacherType = Attacher::AttachEngine3D
  Height = 40
  Placement = pos=(44,19,26) rot=(1,0,0;1.5708rad)
  Radius = 15
FEATURE [Part::Box] Box055  label="Cube051"
  AttacherType = Attacher::AttachEngine3D
  Height = 8
  Length = 5
  Placement = pos=(18.4,-20.7,-3) rot=(0,0,1;0rad)
  Width = 40
FEATURE [Part::FeaturePython] Array  # Draft array (typed FeaturePython)
  Angle = 360
  ArrayType = 0
  Axis = (0,0,1)
  Base = -> Box055
  Center = (0,0,0)
  Fuse = false
  IntervalAxis = (0,0,0)
  IntervalX = (10,0,0)
  IntervalY = (0,1,0)
  IntervalZ = (0,0,1)
  NumberPolar = 0
  NumberX = 5
  NumberY = 0
  NumberZ = 0
  Placement = pos=(-3,0,0) rot=(0,0,1;0rad)
FEATURE [Part::Cut] Cut012
  Base = -> Body020
  Tool = -> Array
FEATURE [Part::Cylinder] Cylinder040
  Angle = 360
  AttacherType = Attacher::AttachEngine3D
  Height = 11
  Placement = pos=(44.6,-3.4,-4.4) rot=(0,0,1;0rad)
  Radius = 1.4
FEATURE [Part::Cylinder] Cylinder041
  Angle = 360
  AttacherType = Attacher::AttachEngine3D
  Height = 11
  Placement = pos=(60.8,-3.4,-4.4) rot=(0,0,1;0rad)
  Radius = 1.4
FEATURE [Sketcher::SketchObject] Sketch024
  MapMode = 5
  Placement = pos=(0,0,0) rot=(0.57735,0.57735,0.57735;2.0944rad)
  Support = -> [YZ_Plane021]
  sketch-geometry (17):
    g0: LineSegment StartX=-31.9997 StartY=8.95013 StartZ=0 EndX=-30.9497 EndY=8.95013 EndZ=0
    g1: LineSegment StartX=-22.9297 StartY=6.95013 StartZ=0 EndX=-24.9997 EndY=6.95013 EndZ=0
    g2: GeomPoint [constr] X=-32 Y=2 Z=0
    g3: LineSegment StartX=-22.9297 StartY=8.95013 StartZ=0 EndX=-22.9297 EndY=7.95013 EndZ=0
    g4: LineSegment StartX=-30.9497 StartY=7.95013 StartZ=0 EndX=-30.9497 EndY=8.95013 EndZ=0
    g5: LineSegment StartX=-22.9297 StartY=8.95013 StartZ=0 EndX=-21.9297 EndY=8.95013 EndZ=0
    g6: LineSegment StartX=-31.9997 StartY=8.95013 StartZ=0 EndX=-31.9997 EndY=1.7 EndZ=0
    g7: LineSegment StartX=-30.3797 StartY=0.8 StartZ=0 EndX=-28.7797 EndY=0.8 EndZ=0
    g8: LineSegment StartX=-28.7797 StartY=0.8 StartZ=0 EndX=-28.7797 EndY=2.4 EndZ=0
    g9: LineSegment StartX=-28.7797 StartY=2.4 StartZ=0 EndX=-25.9797 EndY=2.4 EndZ=0
    g10: LineSegment StartX=-25.9797 StartY=2.4 StartZ=0 EndX=-25.9797 EndY=5.95013 EndZ=0
    g11: ArcOfCircle CenterX=-24.9997 CenterY=5.96993 CenterZ=0 NormalX=0 NormalY=0 NormalZ=1 AngleXU=0 Radius=0.9802 StartAngle=1.5708 EndAngle=3.16179
    g12: ArcOfCircle CenterX=-22.9397 CenterY=7.96013 CenterZ=0 NormalX=0 NormalY=0 NormalZ=1 AngleXU=0 Radius=1.01005 StartAngle=4.72229 EndAngle=6.27328
    g13: LineSegment StartX=-21.9297 StartY=8.95013 StartZ=0 EndX=-21.9297 EndY=7.95013 EndZ=0
    g14: LineSegment StartX=-31.9997 StartY=1.7 StartZ=0 EndX=-30.3797 EndY=1.7 EndZ=0
    g15: LineSegment StartX=-30.3797 StartY=1.7 StartZ=0 EndX=-30.3797 EndY=0.8 EndZ=0
    g16: LineSegment StartX=-22.9297 StartY=7.95013 StartZ=0 EndX=-30.9497 EndY=7.95013 EndZ=0
  constraints (45):
    c: Horizontal(g0)
    c: Horizontal(g1)
    c: Coincident(g16,g4)
    c: Vertical(g3)
    c: Vertical(g4)
    c: Coincident(g0,g4)
    c: Vertical(g6)
    c: Horizontal(g7)
    c: Vertical(g8)
    c: Coincident(g9,g8)
    c: Horizontal(g9)
    c: Coincident(g9,g10)
    c: Coincident(g10,g11)
    c: Coincident(g1,g11)
    c: Coincident(g13,g5)
    c: Coincident(g13,g12)
    c: Vertical(g13)
    c: DistanceX(g3,g5) = 1
    c: DistanceY(g3,g3) = 1
    c: Coincident(g1,g12)
    c: Vertical(g10)
    c: Coincident(g3,g5)
    c: Horizontal(g5)
    c: DistanceY(g4,g4) = 1
    c: Coincident(g7,g8)
    c: DistanceY(g7) = 0.8
    c: Coincident(g14,g15)
    c: Horizontal(g14)
    c: Vertical(g15)
    c: Coincident(g15,g7)
    c: DistanceX(g7,g7) = 1.6
    c: DistanceY(g15,g15) = 0.9
    c: Coincident(g6,g14)
    c: DistanceX(g9,g9) = 2.8
    c: DistanceY(g9) = 2.4
    c: Coincident(g6,g0)
    c: Coincident(g16,g3)
    c: Horizontal(g16)
    c: DistanceX(g16,g16) = 8.02
    c: Distance(g0,g5) = 10.07
    c: DistanceX(g0) = -31.9997
    c: Distance(g10,g6) = 6.02
    c: Distance(g1,g6) = 7
    c: DistanceX(g10,g11) = 0.98
    c: DistanceY(g1,g12) = 1.01
FEATURE [PartDesign::Revolution] Revolution001
  Angle = 360
  Axis = (1.129e-13,1,-1.129e-13)
  Base = (0,0,0)
  Placement = pos=(0,0,0) rot=(0.57735,0.57735,0.57735;2.0944rad)
  Profile = -> Sketch024
  ReferenceAxis = -> Sketch024 [H_Axis]
FEATURE [Sketcher::SketchObject] Sketch025
  Placement = pos=(-5.2,0,0) rot=(1,0,0;1.5708rad)
  sketch-geometry (4):
    g0: ArcOfParabola CenterX=5.222 CenterY=2.57163 CenterZ=0 NormalX=0 NormalY=0 NormalZ=1 Focal=0.62612 AngleXU=1.5708 StartAngle=-2.5 EndAngle=2.5
    g1: GeomPoint X=5.222 Y=3.19775 Z=0
    g2: LineSegment [constr] StartX=5.222 StartY=2.57163 StartZ=0 EndX=5.222 EndY=3.19775 EndZ=0
    g3: ArcOfCircle CenterX=5.222 CenterY=-0.853854 CenterZ=0 NormalX=0 NormalY=0 NormalZ=1 AngleXU=0 Radius=6.42716 StartAngle=1.17128 EndAngle=1.97031
  constraints (8):
    c: InternalAlignment(g1,g0)
    c: Coincident(g1,g2)
    c: Coincident(g0,g2)
    c: Coincident(g0,g3)
    c: Coincident(g3,g0)
    c: DistanceX(g0,g0) = 5
    c: DistanceY(g0,g0) = 0
    c: Symmetric(g0,g0,g2)
FEATURE [PartDesign::Pocket] Pocket001
  BaseFeature = -> Revolution001
  Length = 5
  Length2 = 100
  Midplane = true
  Placement = pos=(0,0,0) rot=(0.57735,0.57735,0.57735;2.0944rad)
  Profile = -> Sketch025
  Type = 1
FEATURE [PartDesign::PolarPattern] PolarPattern001
  Angle = 360
  Axis = -> Y_Axis021
  BaseFeature = -> Pocket001
  Occurrences = 5
  Originals = -> [Pocket001]
  Placement = pos=(0,0,0) rot=(0.57735,0.57735,0.57735;2.0944rad)
FEATURE [PartDesign::Body] Body021  label="03_FrontWheel"
  Group = -> [Sketch024,Revolution001,Sketch025,Pocket001,PolarPattern001]
  Origin = -> Origin021
  Placement = pos=(54.7,7,-10.5) rot=(0,0,1;0rad)
  Tip = -> PolarPattern001
FEATURE [PartDesign::FeatureBase] Clone
  BaseFeature = -> Fusion
  Placement = pos=(0,12,0) rot=(0,1,0;3.14159rad)
FEATURE [PartDesign::Body] Body022  label="Servo9gRight"
  BaseFeature = -> Fusion
  Group = -> [Clone]
  Origin = -> Origin022
  Placement = pos=(0,-1,0) rot=(1,0,0;3.14159rad)
  Tip = -> Clone
FEATURE [Part::Cut] Cut
  Base = -> Fusion014
  Tool = -> Cylinder039
FEATURE [Sketcher::SketchObject] Sketch027
  MapMode = 5
  Support = -> [XY_Plane024]
  sketch-geometry (6):
    g0: LineSegment StartX=11.1661 StartY=12.7923 StartZ=0 EndX=64.95 EndY=12.7923 EndZ=0
    g1: LineSegment StartX=64.95 StartY=12.7923 StartZ=0 EndX=64.95 EndY=-12.7923 EndZ=0
    g2: LineSegment StartX=64.95 StartY=-12.7923 StartZ=0 EndX=11.1661 EndY=-12.7923 EndZ=0
    g3: LineSegment StartX=11.1661 StartY=-12.7923 StartZ=0 EndX=11.1661 EndY=12.7923 EndZ=0
    g4: Circle CenterX=54.7 CenterY=7.8 CenterZ=0 NormalX=0 NormalY=0 NormalZ=1 AngleXU=0 Radius=1
    g5: Circle CenterX=54.7 CenterY=-7.8 CenterZ=0 NormalX=0 NormalY=0 NormalZ=1 AngleXU=0 Radius=1
  constraints (10):
    c: Coincident(g0,g1)
    c: Coincident(g1,g2)
    c: Horizontal(g0)
    c: Horizontal(g2)
    c: Vertical(g3)
    c: Coincident(g2,g3)
    c: Symmetric(g1,g0,g-1)
    c: Coincident(g0,g3)
    c: Distance(g4,g5) = 15.6
    c: Symmetric(g4,g5,g-1)
FEATURE [PartDesign::Pad] Pad022
  Length = 2
  Length2 = 100
  Profile = -> Sketch027
  Type = 0
FEATURE [PartDesign::Body] Body023
  Group = -> [Sketch027,Pad022]
  Origin = -> Origin023
  Placement = pos=(0,0,-6) rot=(0,0,1;0rad)
  Tip = -> Pad022
FEATURE [Part::Fillet] Fillet007
  Base = -> Pad022
  Edges = 3 edges r=1: [Edge3,Edge6,Edge9]
  Placement = pos=(0,0,-8) rot=(0,0,1;0rad)
FEATURE [Part::Cut] Cut013
  Base = -> Fillet007
  Tool = -> Fusion040
FEATURE [Part::Box] Box025  label="Cube022"
  AttacherType = Attacher::AttachEngine3D
  Height = 29
  Length = 25
  Placement = pos=(-13.84,-10.33,0) rot=(0,0,1;0rad)
  Width = 20.56
FEATURE [Sketcher::SketchObject] Sketch028
  MapMode = 5
  Support = -> [XY_Plane025]
  sketch-geometry (9):
    g0: LineSegment StartX=-11.26 StartY=12.2746 StartZ=0 EndX=-11.26 EndY=10.2129 EndZ=0
    g1: LineSegment StartX=-11.26 StartY=10.2129 StartZ=0 EndX=-13.8533 EndY=10.2129 EndZ=0
    g2: LineSegment StartX=-13.8533 StartY=10.2129 StartZ=0 EndX=-13.8533 EndY=-10.2129 EndZ=0
    g3: LineSegment StartX=-13.8533 StartY=-10.2129 StartZ=0 EndX=-11.26 EndY=-10.2129 EndZ=0
    g4: LineSegment StartX=-11.26 StartY=-10.2129 StartZ=0 EndX=-11.26 EndY=-12.2746 EndZ=0
    g5: LineSegment StartX=-11.26 StartY=-12.2746 StartZ=0 EndX=-16 EndY=-12.2746 EndZ=0
    g6: LineSegment StartX=-16 StartY=-12.2746 StartZ=0 EndX=-16 EndY=12.2746 EndZ=0
    g7: LineSegment StartX=-16 StartY=12.2746 StartZ=0 EndX=-11.26 EndY=12.2746 EndZ=0
    g8: LineSegment StartX=-11.26 StartY=12.2746 StartZ=0 EndX=-11.26 EndY=10.2129 EndZ=0
  constraints (24):
    c: Vertical(g0)
    c: Coincident(g0,g1)
    c: Horizontal(g1)
    c: Coincident(g1,g2)
    c: Vertical(g2)
    c: Coincident(g2,g3)
    c: Horizontal(g3)
    c: Coincident(g3,g4)
    c: Coincident(g4,g5)
    c: Horizontal(g5)
    c: Coincident(g5,g6)
    c: Coincident(g6,g7)
    c: Horizontal(g7)
    c: Coincident(g7,g8)
    c: Coincident(g8,g0)
    c: Vertical(g8)
    c: Symmetric(g6,g5,g-1)
    c: Symmetric(g0,g4,g-1)
    c: Equal(g1,g3)
    c: Equal(g0,g4)
    c: DistanceX(g6) = -16
    c: DistanceY(g6) = 12.2746
    c: DistanceX(g1) = -13.8533
    c: DistanceY(g1) = 10.2129
FEATURE [PartDesign::Pad] Pad023
  Length = 19.5
  Length2 = 100
  Profile = -> Sketch028
  Type = 0
FEATURE [PartDesign::Body] Body024
  Group = -> [Sketch028,Pad023]
  Origin = -> Origin024
  Placement = pos=(0,0,6.5) rot=(0,0,1;0rad)
  Tip = -> Pad023
FEATURE [Part::Box] Box057  label="Cube053"
  AttacherType = Attacher::AttachEngine3D
  Height = 5
  Length = 5
  Placement = pos=(8.96,-8.03,4) rot=(0,0,1;0rad)
  Width = 16
FEATURE [Part::MultiFuse] Fusion044
  Shapes = -> [Box057,Box022,Box025]
FEATURE [Part::Cut] Cut014
  Base = -> Cut
  Tool = -> Fusion044
FEATURE [Part::MultiFuse] Fusion045  label="01_Chassis"
  Shapes = -> [Cut007,Box026,Fillet005,Cut012,Cut010,Chamfer005,Body024,Cut013,Cut014]
FEATURE [Sketcher::SketchObject] Sketch029
  MapMode = 5
  Support = -> [XY_Plane026]
  sketch-geometry (20):
    g0: LineSegment StartX=-11.26 StartY=20.5 StartZ=0 EndX=-11.26 EndY=10.2128 EndZ=0
    g1: LineSegment StartX=-11.26 StartY=10.2128 StartZ=0 EndX=-13.853 EndY=10.2128 EndZ=0
    g2: LineSegment StartX=-13.853 StartY=10.2128 StartZ=0 EndX=-13.853 EndY=-10.2128 EndZ=0
    g3: LineSegment StartX=63.2 StartY=11 StartZ=0 EndX=24 EndY=11 EndZ=0
    g4: LineSegment StartX=13 StartY=11 StartZ=0 EndX=13 EndY=7.97 EndZ=0
    g5: LineSegment StartX=13 StartY=7.97 StartZ=0 EndX=11.48 EndY=7.97 EndZ=0
    g6: LineSegment StartX=11.48 StartY=7.97 StartZ=0 EndX=11.48 EndY=20.5 EndZ=0
    g7: LineSegment StartX=11.48 StartY=20.5 StartZ=0 EndX=-11.26 EndY=20.5 EndZ=0
    g8: LineSegment StartX=-11.26 StartY=-20.5 StartZ=0 EndX=-11.26 EndY=-10.2128 EndZ=0
    g9: LineSegment StartX=-11.26 StartY=-10.2128 StartZ=0 EndX=-13.853 EndY=-10.2128 EndZ=0
    g10: LineSegment StartX=63.2 StartY=11 StartZ=0 EndX=63.2 EndY=-11 EndZ=0
    g11: LineSegment StartX=63.2 StartY=-11 StartZ=0 EndX=24 EndY=-11 EndZ=0
    g12: LineSegment StartX=13 StartY=-11 StartZ=0 EndX=13 EndY=-7.97 EndZ=0
    g13: LineSegment StartX=13 StartY=-7.97 StartZ=0 EndX=11.48 EndY=-7.97 EndZ=0
    g14: LineSegment StartX=11.48 StartY=-7.97 StartZ=0 EndX=11.48 EndY=-20.5 EndZ=0
    g15: LineSegment StartX=11.48 StartY=-20.5 StartZ=0 EndX=-11.26 EndY=-20.5 EndZ=0
    g16: ArcOfCircle CenterX=20 CenterY=11 CenterZ=0 NormalX=0 NormalY=0 NormalZ=1 AngleXU=0 Radius=4 StartAngle=3.14159 EndAngle=6.28319
    g17: LineSegment StartX=16 StartY=11 StartZ=0 EndX=13 EndY=11 EndZ=0
    g18: ArcOfCircle CenterX=20 CenterY=-11 CenterZ=0 NormalX=0 NormalY=0 NormalZ=1 AngleXU=0 Radius=4 StartAngle=4e-16 EndAngle=3.14159
    g19: LineSegment StartX=16 StartY=-11 StartZ=0 EndX=13 EndY=-11 EndZ=0
  constraints (38):
    c: Vertical(g0)
    c: Coincident(g0,g1)
    c: Horizontal(g1)
    c: Coincident(g1,g2)
    c: Vertical(g2)
    c: Horizontal(g3)
    c: Coincident(g17,g4)
    c: Vertical(g4)
    c: Coincident(g4,g5)
    c: Horizontal(g5)
    c: Coincident(g5,g6)
    c: Vertical(g6)
    c: Coincident(g6,g7)
    c: PointOnObject(g7,g0)
    c: Horizontal(g7)
    c: Vertical(g8)
    c: Coincident(g8,g9)
    c: Horizontal(g9)
    c: Vertical(g10)
    c: Coincident(g10,g11)
    c: Horizontal(g11)
    c: Coincident(g19,g12)
    c: Vertical(g12)
    c: Coincident(g12,g13)
    c: Horizontal(g13)
    c: Coincident(g13,g14)
    c: Vertical(g14)
    c: Coincident(g14,g15)
    c: PointOnObject(g15,g8)
    c: Horizontal(g15)
    c: Coincident(g2,g9)
    c: Coincident(g3,g10)
    c: Tangent(g3,g17)
    c: Coincident(g16,g17)
    c: Coincident(g16,g3)
    c: PointOnObject(g11,g18)
    c: PointOnObject(g19,g18)
    c: Tangent(g11,g19)
FEATURE [PartDesign::Pad] Pad024
  Length = 2
  Length2 = 100
  Profile = -> Sketch029
  Type = 0
FEATURE [PartDesign::Body] Body025
  Group = -> [Sketch029,Pad024]
  Origin = -> Origin025
  Placement = pos=(0,0,6) rot=(0,0,1;0rad)
  Tip = -> Pad024
FEATURE [App::DocumentObjectGroup] Group  label="Resources"
  Group = -> [Box,Fusion,Fusion003,ImagePlane,ImagePlane002,Body014,Fusion006,Box007,Fusion037,SmartCars,SmartCars001,Body022,ImagePlane001,Rectangle,Body023,Body025,XY_Plane027]
FEATURE [Part::Cylinder] Cylinder042
  Angle = 360
  AttacherType = Attacher::AttachEngine3D
  Height = 11
  Placement = pos=(37.6,8.5,-4.4) rot=(0,0,1;0rad)
  Radius = 1.4
FEATURE [Part::Cylinder] Cylinder043
  Angle = 360
  AttacherType = Attacher::AttachEngine3D
  Height = 11
  Placement = pos=(30.3,-6.3,-4.4) rot=(0,0,1;0rad)
  Radius = 1.4
FEATURE [Part::Box] Box058  label="Cube054"
  AttacherType = Attacher::AttachEngine3D
  Height = 4
  Length = 15
  Placement = pos=(-7.4,-1,2) rot=(0,0,1;0rad)
  Width = 2
FEATURE [Part::Fillet] Fillet008
  Base = -> Box058
  Edges = 4 edges r=0.5: [Edge4,Edge8,Edge9,Edge11]
FEATURE [Part::Chamfer] Chamfer006
  Base = -> Pad024
  Edges = 20 edges r=1: [Edge3,Edge6,Edge9,Edge12,Edge15,Edge18,Edge21,Edge24,Edge27,Edge30,Edge33,Edge36,Edge39,Edge42,Edge45,Edge48,Edge51,Edge54,Edge57,Edge59]
  Placement = pos=(0,0,6) rot=(0,0,1;0rad)
FEATURE [Part::MultiFuse] Fusion046  label="05_PCBCoverNormal"
  Shapes = -> [Cylinder041,Cylinder040,Cylinder043,Cylinder042,Fillet008,Chamfer006]
FEATURE [Part::Cylinder] Cylinder044
  Angle = 360
  AttacherType = Attacher::AttachEngine3D
  Height = 11
  Placement = pos=(44.6,-3.4,-4.4) rot=(0,0,1;0rad)
  Radius = 1.4
FEATURE [Part::Cylinder] Cylinder045
  Angle = 360
  AttacherType = Attacher::AttachEngine3D
  Height = 11
  Placement = pos=(60.8,-3.4,-4.4) rot=(0,0,1;0rad)
  Radius = 1.4
FEATURE [Part::Box] Box059  label="Cube055"
  AttacherType = Attacher::AttachEngine3D
  Height = 4
  Length = 15
  Placement = pos=(-7.4,-2.25,2) rot=(0,0,1;0rad)
  Width = 4.5
FEATURE [Part::Cylinder] Cylinder046
  Angle = 360
  AttacherType = Attacher::AttachEngine3D
  Height = 11
  Placement = pos=(30.3,-6.3,-4.4) rot=(0,0,1;0rad)
  Radius = 1.4
FEATURE [Part::Cylinder] Cylinder047
  Angle = 360
  AttacherType = Attacher::AttachEngine3D
  Height = 11
  Placement = pos=(37.6,8.5,-4.4) rot=(0,0,1;0rad)
  Radius = 1.4
FEATURE [Sketcher::SketchObject] Sketch030
  MapMode = 5
  Support = -> [XY_Plane027]
  sketch-geometry (20):
    g0: LineSegment StartX=-11.26 StartY=20.5 StartZ=0 EndX=-11.26 EndY=10.2128 EndZ=0
    g1: LineSegment StartX=-11.26 StartY=10.2128 StartZ=0 EndX=-13.853 EndY=10.2128 EndZ=0
    g2: LineSegment StartX=-13.853 StartY=10.2128 StartZ=0 EndX=-13.853 EndY=-10.2128 EndZ=0
    g3: LineSegment StartX=63.2 StartY=11 StartZ=0 EndX=24 EndY=11 EndZ=0
    g4: LineSegment StartX=13 StartY=11 StartZ=0 EndX=13 EndY=7.97 EndZ=0
    g5: LineSegment StartX=13 StartY=7.97 StartZ=0 EndX=11.48 EndY=7.97 EndZ=0
    g6: LineSegment StartX=11.48 StartY=7.97 StartZ=0 EndX=11.48 EndY=20.5 EndZ=0
    g7: LineSegment StartX=11.48 StartY=20.5 StartZ=0 EndX=-11.26 EndY=20.5 EndZ=0
    g8: LineSegment StartX=-11.26 StartY=-20.5 StartZ=0 EndX=-11.26 EndY=-10.2128 EndZ=0
    g9: LineSegment StartX=-11.26 StartY=-10.2128 StartZ=0 EndX=-13.853 EndY=-10.2128 EndZ=0
    g10: LineSegment StartX=63.2 StartY=11 StartZ=0 EndX=63.2 EndY=-11 EndZ=0
    g11: LineSegment StartX=63.2 StartY=-11 StartZ=0 EndX=24 EndY=-11 EndZ=0
    g12: LineSegment StartX=13 StartY=-11 StartZ=0 EndX=13 EndY=-7.97 EndZ=0
    g13: LineSegment StartX=13 StartY=-7.97 StartZ=0 EndX=11.48 EndY=-7.97 EndZ=0
    g14: LineSegment StartX=11.48 StartY=-7.97 StartZ=0 EndX=11.48 EndY=-20.5 EndZ=0
    g15: LineSegment StartX=11.48 StartY=-20.5 StartZ=0 EndX=-11.26 EndY=-20.5 EndZ=0
    g16: ArcOfCircle CenterX=20 CenterY=11 CenterZ=0 NormalX=0 NormalY=0 NormalZ=1 AngleXU=0 Radius=4 StartAngle=3.14159 EndAngle=6.28319
    g17: LineSegment StartX=16 StartY=11 StartZ=0 EndX=13 EndY=11 EndZ=0
    g18: ArcOfCircle CenterX=20 CenterY=-11 CenterZ=0 NormalX=0 NormalY=0 NormalZ=1 AngleXU=0 Radius=4 StartAngle=4e-16 EndAngle=3.14159
    g19: LineSegment StartX=16 StartY=-11 StartZ=0 EndX=13 EndY=-11 EndZ=0
  constraints (38):
    c: Vertical(g0)
    c: Coincident(g0,g1)
    c: Horizontal(g1)
    c: Coincident(g1,g2)
    c: Vertical(g2)
    c: Horizontal(g3)
    c: Coincident(g17,g4)
    c: Vertical(g4)
    c: Coincident(g4,g5)
    c: Horizontal(g5)
    c: Coincident(g5,g6)
    c: Vertical(g6)
    c: Coincident(g6,g7)
    c: PointOnObject(g7,g0)
    c: Horizontal(g7)
    c: Vertical(g8)
    c: Coincident(g8,g9)
    c: Horizontal(g9)
    c: Vertical(g10)
    c: Coincident(g10,g11)
    c: Horizontal(g11)
    c: Coincident(g19,g12)
    c: Vertical(g12)
    c: Coincident(g12,g13)
    c: Horizontal(g13)
    c: Coincident(g13,g14)
    c: Vertical(g14)
    c: Coincident(g14,g15)
    c: PointOnObject(g15,g8)
    c: Horizontal(g15)
    c: Coincident(g2,g9)
    c: Coincident(g3,g10)
    c: Tangent(g3,g17)
    c: Coincident(g16,g17)
    c: Coincident(g16,g3)
    c: PointOnObject(g11,g18)
    c: PointOnObject(g19,g18)
    c: Tangent(g11,g19)
FEATURE [PartDesign::Pad] Pad025
  Length = 2
  Length2 = 100
  Profile = -> Sketch030
  Type = 0
FEATURE [Part::Chamfer] Chamfer007
  Base = -> Pad025
  Edges = 20 edges r=1: [Edge3,Edge6,Edge9,Edge12,Edge15,Edge18,Edge21,Edge24,Edge27,Edge30,Edge33,Edge36,Edge39,Edge42,Edge45,Edge48,Edge51,Edge54,Edge57,Edge59]
  Placement = pos=(0,0,6) rot=(0,0,1;0rad)
FEATURE [Part::Fillet] Fillet009
  Base = -> Box059
  Edges = 4 edges r=0.5: [Edge4,Edge8,Edge9,Edge11]
FEATURE [Part::MultiFuse] Fusion047  label="04_PCBCoverBig"
  Shapes = -> [Cylinder045,Cylinder044,Cylinder046,Cylinder047,Fillet009,Chamfer007]
